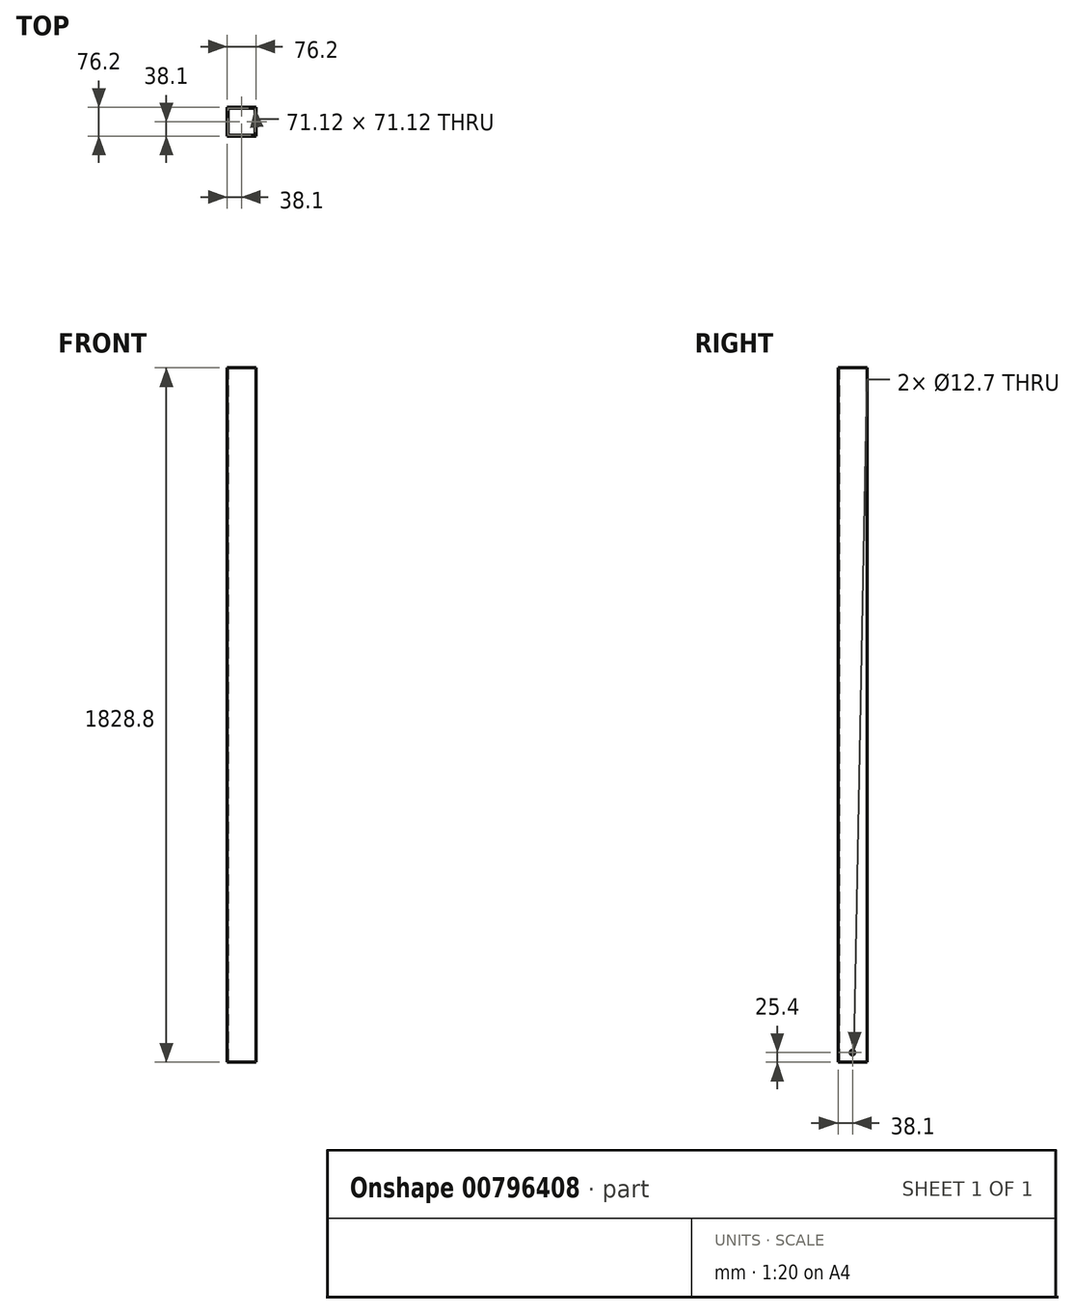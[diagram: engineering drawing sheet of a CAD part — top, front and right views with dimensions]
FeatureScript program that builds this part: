
annotation { "Feature Type Name" : "Feature", "Feature Type Description" : "" }
export const myFeature = defineFeature(function(context is Context, id is Id, definition is map)
    precondition{}
    {
        {
            var Q0;
            Q0=qCreatedBy(makeId("Top.planeOp"),FACE);
            var sketch = newSketch(context, id + "F0", { "sketchPlane" : qUnion([Q0])});
            skLineSegment(sketch, "E0.bottom", {"start": v(0, 0) * mm, "end": v(0, 0) * mm});
            skLineSegment(sketch, "E0.top", {"start": v(0, 0) * mm, "end": v(0, 0) * mm});
            skLineSegment(sketch, "E0.left", {"start": v(0, 0) * mm, "end": v(0, 0) * mm});
            skLineSegment(sketch, "E0.right", {"start": v(0, 0) * mm, "end": v(0, 0) * mm});
            skPoint(sketch, "E0.middle", {"position": v(0, 0) * mm});
            skLineSegment(sketch, "E1.bottom", {"start": v(38.1, -38.1) * mm, "end": v(-38.1, -38.1) * mm});
            skLineSegment(sketch, "E1.top", {"start": v(38.1, 38.1) * mm, "end": v(-38.1, 38.1) * mm});
            skLineSegment(sketch, "E1.left", {"start": v(38.1, -38.1) * mm, "end": v(38.1, 38.1) * mm});
            skLineSegment(sketch, "E1.right", {"start": v(-38.1, -38.1) * mm, "end": v(-38.1, 38.1) * mm});
            skLineSegment(sketch, "E2.0", {"start": v(35.56, 35.56) * mm, "end": v(-35.56, 35.56) * mm});
            skLineSegment(sketch, "E2.1", {"start": v(35.56, -35.56) * mm, "end": v(35.56, 35.56) * mm});
            skLineSegment(sketch, "E2.2", {"start": v(35.56, -35.56) * mm, "end": v(-35.56, -35.56) * mm});
            skLineSegment(sketch, "E2.3", {"start": v(-35.56, -35.56) * mm, "end": v(-35.56, 35.56) * mm});
            skSolve(sketch);
        }
        {
            var Q0;
            Q0=makeQuery(id+"F0.imprint","IMPRINT",FACE,{"disambiguationData":[TD([[makeQuery(id+"F0.imprint","IMPRINT",EDGE,{"derivedFrom":sQuery(id+"F0.wireOp",EDGE,"E1.bottom")}),-1.0]])]});
            extrude(context, id + "F1", {"entities" : qUnion([Q0]), "depth" : 1828.8 * mm, "offsetDistance" : 25.4 * mm});
        }
        {
            var Q0;
            Q0=makeQuery(id+"F1.opExtrude","SWEPT_FACE",FACE,{"disambiguationData":[OSD([sQuery(id+"F0.wireOp",EDGE,"E1.right")])]});
            var sketch = newSketch(context, id + "F2", { "sketchPlane" : qUnion([Q0])});
            skPoint(sketch, "E3", {"position": v(0, 25.4) * mm});
            skSolve(sketch);
        }
        {
            var Q0;
            Q0=sQuery(id+"F2.wireOp",VERTEX,"E3");
            var Q1;
            Q1=makeQuery(id+"F1.opExtrude","SWEPT_BODY",BODY,{"disambiguationData":[OSD([sQuery(id+"F0.wireOp",EDGE,"E1.bottom"),sQuery(id+"F0.wireOp",EDGE,"E1.top"),sQuery(id+"F0.wireOp",EDGE,"E1.left"),sQuery(id+"F0.wireOp",EDGE,"E1.right"),sQuery(id+"F0.wireOp",EDGE,"E2.0"),sQuery(id+"F0.wireOp",EDGE,"E2.1"),sQuery(id+"F0.wireOp",EDGE,"E2.2"),sQuery(id+"F0.wireOp",EDGE,"E2.3")])]});
            hole(context, id + "F3", {"style" : HoleStyle.SIMPLE, "endStyle" : HoleEndStyle.THROUGH, "holeDiameter" : 12.7 * mm, "majorDiameter" : 6.35 * mm, "isTappedThrough" : true, "tappedDepth" : 12.7 * mm, "tapClearance" : 3, "locations" : qUnion([Q0]), "scope" : qUnion([Q1])});
        }
    });
